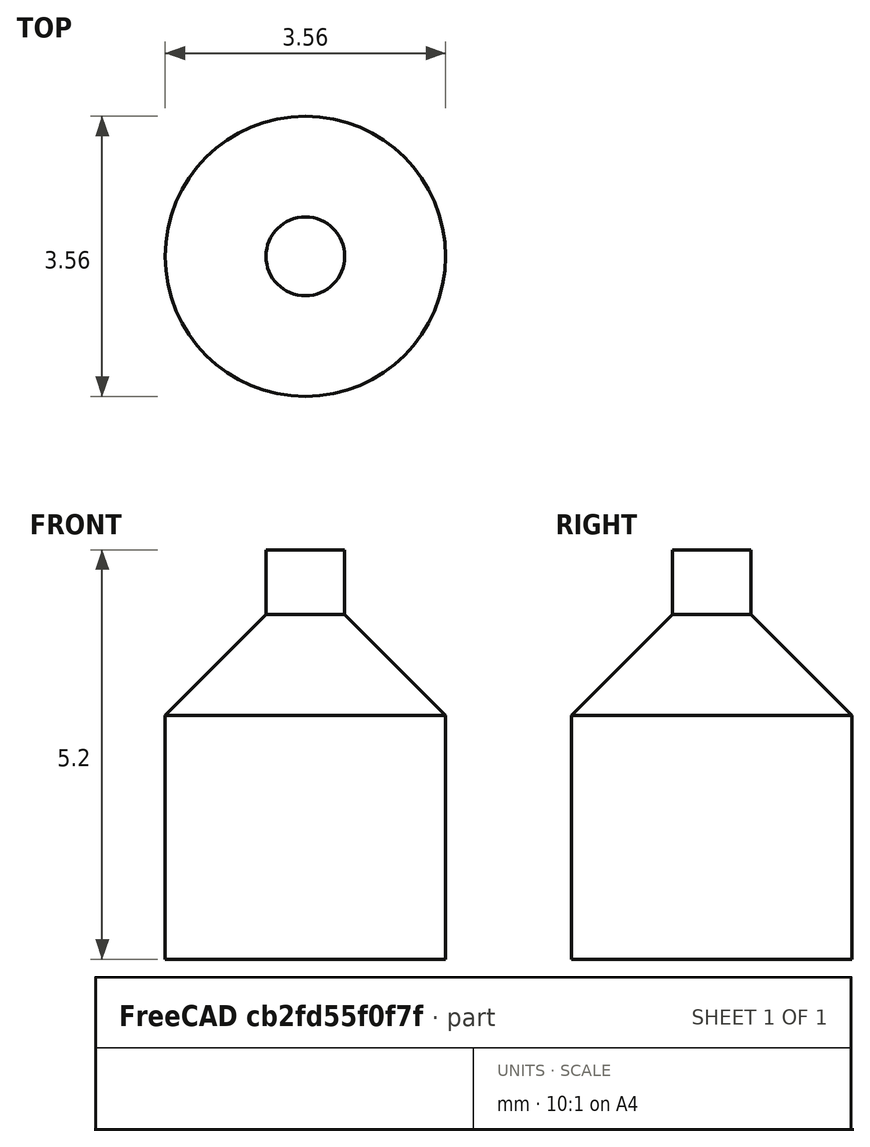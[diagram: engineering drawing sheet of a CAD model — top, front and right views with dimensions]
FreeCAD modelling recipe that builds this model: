
FCSTD DOCUMENT  (FreeCAD 2023.1102R14555 (Git shallow))
Label: LED-plug
License: All rights reserved
LicenseURL: https://en.wikipedia.org/wiki/All_rights_reserved
objects: Sketcher::SketchObject×1, PartDesign::Revolution×1, PartDesign::Body×1
note: 6 computed .brp shape members not serialized (recipe doc carries the construction recipe); baked Part::Feature solids carry a one-line shape summary decoded from their .brp

FEATURE [Sketcher::SketchObject] Sketch
  ArcFitTolerance = 1e-06
  AttachmentSupport = -> [XZ_Plane]
  ExternalBSplineMaxDegree = 5
  ExternalBSplineTolerance = 0.0001
  FullyConstrained = true
  InternalTolerance = 1e-06
  InvalidShape = false
  MakeInternals = false
  MapMode = 5
  Placement = pos=(0,0,0) rot=(1,0,0;1.5708rad)
  Support = -> [XZ_Plane]
  TreeRank = 11
  ValidateShape = false
  sketch-geometry (6):
    g0: LineSegment StartX=0 StartY=0 StartZ=0 EndX=-1.78 EndY=0 EndZ=0
    g1: LineSegment StartX=-1.78 StartY=0 StartZ=0 EndX=-1.78 EndY=3.1 EndZ=0
    g2: LineSegment StartX=-1.78 StartY=3.1 StartZ=0 EndX=-0.5 EndY=4.38 EndZ=0
    g3: LineSegment StartX=-0.5 StartY=4.38 StartZ=0 EndX=-0.5 EndY=5.2 EndZ=0
    g4: LineSegment StartX=-0.5 StartY=5.2 StartZ=0 EndX=0 EndY=5.2 EndZ=0
    g5: LineSegment StartX=0 StartY=5.2 StartZ=0 EndX=0 EndY=0 EndZ=0
  constraints (17):
    c: Coincident(g-1,g0)
    c: PointOnObject(g0,g-1)
    c: Coincident(g0,g1)
    c: Vertical(g1)
    c: Coincident(g1,g2)
    c: Coincident(g2,g3)
    c: Vertical(g3)
    c: Coincident(g3,g4)
    c: PointOnObject(g4,g-2)
    c: Horizontal(g4)
    c: Coincident(g4,g5)
    c: Coincident(g5,g0)
    c: DistanceX(g4,g4) = 0.5
    c: DistanceX(g0,g0) = 1.78
    c: DistanceY(g1,g1) = 3.1
    c: Angle(g-1,g2) = 0.785398
    c: DistanceY(g5,g5) = 5.2
FEATURE [PartDesign::Revolution] Revolution
  AddSubType = 0
  Angle = 360
  Axis = (0,-2e-16,1)
  Base = (0,0,0)
  ClaimChildren = false
  Fit = 0
  FitJoin = 0
  InnerFit = 0
  InnerFitJoin = 0
  InvalidShape = false
  Linearize = true
  NewSolid = false
  Profile = -> Sketch
  ReferenceAxis = -> Sketch [V_Axis]
  Suppress = false
  TreeRank = 12
  ValidateShape = true
  _ProfileBasedVersion = 1
FEATURE [PartDesign::Body] Body
  AutoGroupSolids = false
  ClaimAllChildren = false
  ExportMode = 0
  Group = -> [Sketch,Revolution]
  InvalidShape = false
  Origin = -> Origin
  Tip = -> Revolution
  TreeRank = 10
  ValidateShape = false
  _ExportChildren = -> [Revolution]
  _GroupVersion = 1
